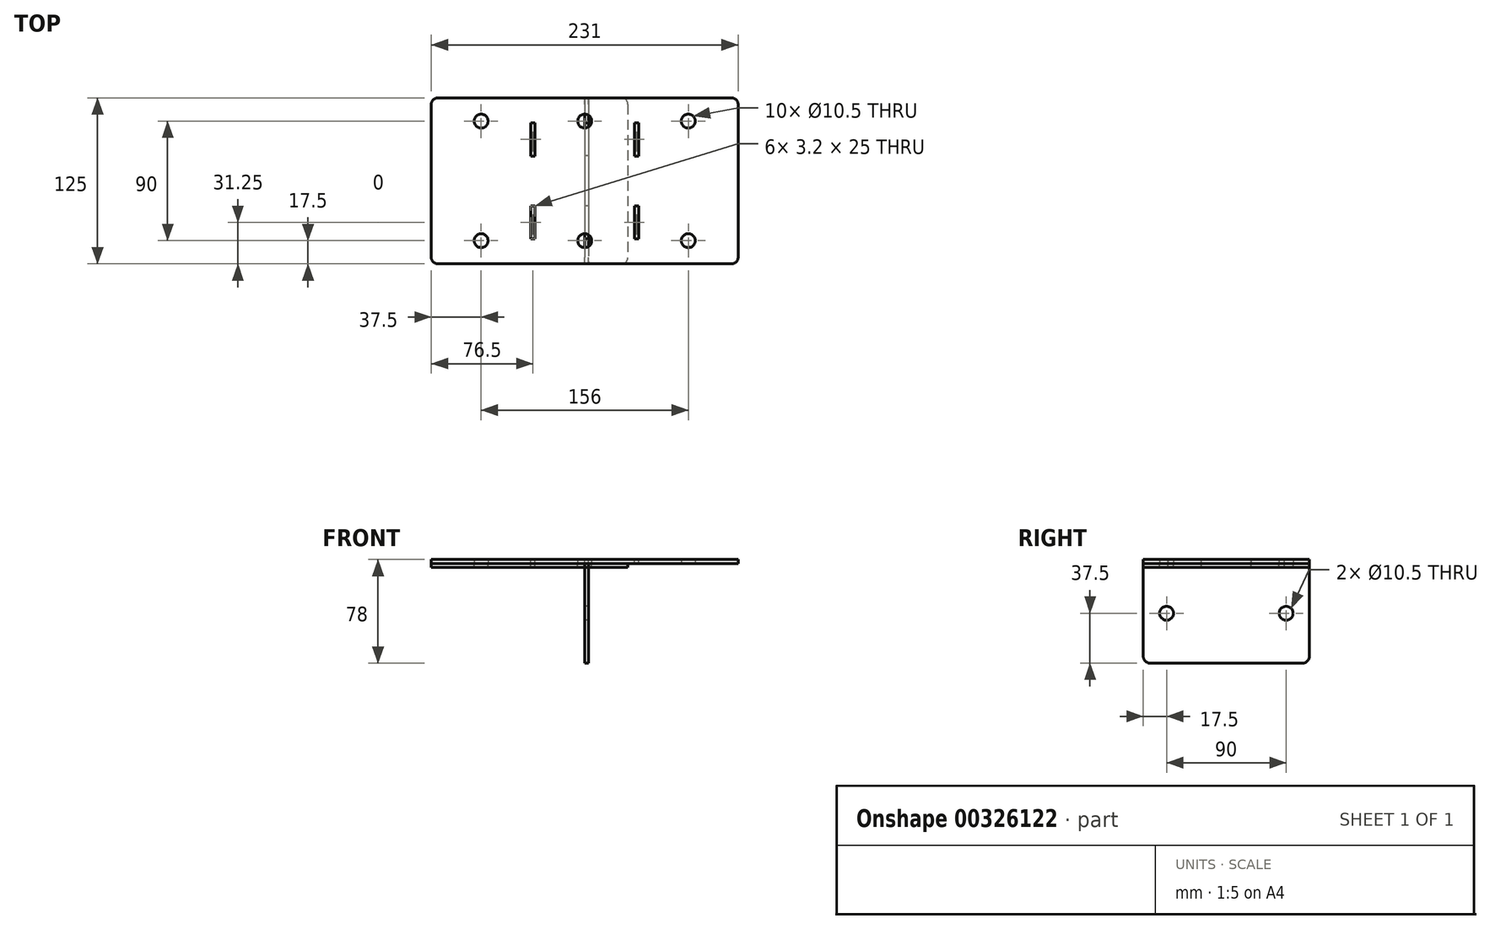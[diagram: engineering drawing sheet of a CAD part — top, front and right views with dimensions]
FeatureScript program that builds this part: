
annotation { "Feature Type Name" : "Feature", "Feature Type Description" : "" }
export const myFeature = defineFeature(function(context is Context, id is Id, definition is map)
    precondition{}
    {
        {
            var Q0;
            Q0=qCreatedBy(makeId("Top.planeOp"),FACE);
            var sketch = newSketch(context, id + "F0", { "sketchPlane" : qUnion([Q0])});
            skLineSegment(sketch, "E0.bottom", {"start": v(-115.5, 62.5) * mm, "end": v(115.5, 62.5) * mm});
            skLineSegment(sketch, "E0.top", {"start": v(-115.5, -62.5) * mm, "end": v(115.5, -62.5) * mm});
            skLineSegment(sketch, "E0.left", {"start": v(-115.5, 62.5) * mm, "end": v(-115.5, -62.5) * mm});
            skLineSegment(sketch, "E0.right", {"start": v(115.5, 62.5) * mm, "end": v(115.5, -62.5) * mm});
            skPoint(sketch, "E0.middle", {"position": v(0, 0) * mm});
            skCircle(sketch, "E1", {"center": v(0, 45) * mm, "radius": 5.25 * mm});
            skCircle(sketch, "E2", {"center": v(0, -45) * mm, "radius": 5.25 * mm});
            skCircle(sketch, "E3", {"center": v(-78, 45) * mm, "radius": 5.25 * mm});
            skCircle(sketch, "E4", {"center": v(-78, -45) * mm, "radius": 5.25 * mm});
            skCircle(sketch, "E5", {"center": v(78, 45) * mm, "radius": 5.25 * mm});
            skCircle(sketch, "E6", {"center": v(78, -45) * mm, "radius": 5.25 * mm});
            skLineSegment(sketch, "E7", {"start": v(0, 62.5) * mm, "end": v(0, -62.5) * mm});
            skLineSegment(sketch, "E8", {"start": v(-115.5, 0) * mm, "end": v(115.5, 0) * mm});
            skSolve(sketch);
        }
        {
            var Q0;
            Q0=makeQuery(id+"F0.imprint","IMPRINT",FACE,{"disambiguationData":[TD([[makeQuery(id+"F0.imprint","IMPRINT",EDGE,{"derivedFrom":sQuery(id+"F0.wireOp",EDGE,"E4")}),-1.0]])]});
            var Q1;
            Q1=makeQuery(id+"F0.imprint","IMPRINT",FACE,{"disambiguationData":[TD([[makeQuery(id+"F0.imprint","IMPRINT",EDGE,{"derivedFrom":sQuery(id+"F0.wireOp",EDGE,"E6")}),-1.0]])]});
            var Q2;
            Q2=makeQuery(id+"F0.imprint","IMPRINT",FACE,{"disambiguationData":[TD([[makeQuery(id+"F0.imprint","IMPRINT",EDGE,{"derivedFrom":sQuery(id+"F0.wireOp",EDGE,"E5")}),-1.0]])]});
            var Q3;
            Q3=makeQuery(id+"F0.imprint","IMPRINT",FACE,{"disambiguationData":[TD([[makeQuery(id+"F0.imprint","IMPRINT",EDGE,{"derivedFrom":sQuery(id+"F0.wireOp",EDGE,"E3")}),-1.0]])]});
            extrude(context, id + "F1", {"entities" : qUnion([Q0, Q1, Q2, Q3]), "depth" : 3 * mm});
        }
        {
            var Q0;
            Q0=makeQuery(id+"F1.opExtrude","CAP_FACE",FACE,{"disambiguationData":[OSD([sQuery(id+"F0.wireOp",EDGE,"E0.bottom"),sQuery(id+"F0.wireOp",EDGE,"E0.top"),sQuery(id+"F0.wireOp",EDGE,"E0.left"),sQuery(id+"F0.wireOp",EDGE,"E0.right"),sQuery(id+"F0.wireOp",EDGE,"E1"),sQuery(id+"F0.wireOp",EDGE,"E2"),sQuery(id+"F0.wireOp",EDGE,"E3"),sQuery(id+"F0.wireOp",EDGE,"E4"),sQuery(id+"F0.wireOp",EDGE,"E5"),sQuery(id+"F0.wireOp",EDGE,"E6")])],"isStart":false});
            var sketch = newSketch(context, id + "F2", { "sketchPlane" : qUnion([Q0])});
            skPoint(sketch, "E9.middle", {"position": v(0, 0) * mm});
            skLineSegment(sketch, "E10.bottom", {"start": v(-37.4, 43.75) * mm, "end": v(-40.6, 43.75) * mm});
            skLineSegment(sketch, "E10.top", {"start": v(-37.4, 18.75) * mm, "end": v(-40.6, 18.75) * mm});
            skLineSegment(sketch, "E10.left", {"start": v(-37.4, 43.75) * mm, "end": v(-37.4, 18.75) * mm});
            skLineSegment(sketch, "E10.right", {"start": v(-40.6, 43.75) * mm, "end": v(-40.6, 18.75) * mm});
            skPoint(sketch, "E10.middle", {"position": v(-39, 31.25) * mm});
            skLineSegment(sketch, "E11.MirrorCS", {"start": v(-37.4, -18.75) * mm, "end": v(-40.6, -18.75) * mm});
            skLineSegment(sketch, "E12.MirrorCS", {"start": v(-37.4, -43.75) * mm, "end": v(-40.6, -43.75) * mm});
            skLineSegment(sketch, "E13.MirrorCS", {"start": v(-37.4, -43.75) * mm, "end": v(-37.4, -18.75) * mm});
            skLineSegment(sketch, "E14.MirrorCS", {"start": v(-40.6, -43.75) * mm, "end": v(-40.6, -18.75) * mm});
            skLineSegment(sketch, "E15.MirrorCS", {"start": v(37.4, -43.75) * mm, "end": v(40.6, -43.75) * mm});
            skLineSegment(sketch, "E16.MirrorCS", {"start": v(37.4, -43.75) * mm, "end": v(37.4, -18.75) * mm});
            skLineSegment(sketch, "E17.MirrorCS", {"start": v(40.6, -43.75) * mm, "end": v(40.6, -18.75) * mm});
            skLineSegment(sketch, "E18.MirrorCS", {"start": v(37.4, -18.75) * mm, "end": v(40.6, -18.75) * mm});
            skLineSegment(sketch, "E19.MirrorCS", {"start": v(37.4, 18.75) * mm, "end": v(40.6, 18.75) * mm});
            skLineSegment(sketch, "E20.MirrorCS", {"start": v(37.4, 43.75) * mm, "end": v(37.4, 18.75) * mm});
            skLineSegment(sketch, "E21.MirrorCS", {"start": v(40.6, 43.75) * mm, "end": v(40.6, 18.75) * mm});
            skLineSegment(sketch, "E22.MirrorCS", {"start": v(37.4, 43.75) * mm, "end": v(40.6, 43.75) * mm});
            skSolve(sketch);
        }
        {
            var Q0;
            Q0=makeQuery(id+"F2.imprint","IMPRINT",FACE,{"disambiguationData":[TD([[makeQuery(id+"F2.imprint","IMPRINT",EDGE,{"derivedFrom":sQuery(id+"F2.wireOp",EDGE,"E19.MirrorCS")}),1.0]])]});
            var Q1;
            Q1=makeQuery(id+"F2.imprint","IMPRINT",FACE,{"disambiguationData":[TD([[makeQuery(id+"F2.imprint","IMPRINT",EDGE,{"derivedFrom":sQuery(id+"F2.wireOp",EDGE,"E10.bottom")}),1.0]])]});
            var Q2;
            Q2=makeQuery(id+"F2.imprint","IMPRINT",FACE,{"disambiguationData":[TD([[makeQuery(id+"F2.imprint","IMPRINT",EDGE,{"derivedFrom":sQuery(id+"F2.wireOp",EDGE,"E15.MirrorCS")}),1.0]])]});
            var Q3;
            Q3=makeQuery(id+"F2.imprint","IMPRINT",FACE,{"disambiguationData":[TD([[makeQuery(id+"F2.imprint","IMPRINT",EDGE,{"derivedFrom":sQuery(id+"F2.wireOp",EDGE,"E11.MirrorCS")}),1.0]])]});
            extrude(context, id + "F3", {"entities" : qUnion([Q0, Q1, Q2, Q3]), "operationType" : NewBodyOperationType.REMOVE, "oppositeDirection" : true, "depth" : 25 * mm});
        }
        {
            var Q0;
            Q0=makeQuery(id+"F1.opExtrude","SWEPT_EDGE",EDGE,{"disambiguationData":[OSD([sQuery(id+"F0.wireOp",EDGE,"E0.bottom"),sQuery(id+"F0.wireOp",EDGE,"E0.right")])]});
            var Q1;
            Q1=makeQuery(id+"F1.opExtrude","SWEPT_EDGE",EDGE,{"disambiguationData":[OSD([sQuery(id+"F0.wireOp",EDGE,"E0.top"),sQuery(id+"F0.wireOp",EDGE,"E0.right")])]});
            var Q2;
            Q2=makeQuery(id+"F1.opExtrude","SWEPT_EDGE",EDGE,{"disambiguationData":[OSD([sQuery(id+"F0.wireOp",EDGE,"E0.bottom"),sQuery(id+"F0.wireOp",EDGE,"E0.left")])]});
            var Q3;
            Q3=makeQuery(id+"F1.opExtrude","SWEPT_EDGE",EDGE,{"disambiguationData":[OSD([sQuery(id+"F0.wireOp",EDGE,"E0.top"),sQuery(id+"F0.wireOp",EDGE,"E0.left")])]});
            fillet(context, id + "F4", {"entities" : qUnion([Q0, Q1, Q2, Q3]), "radius" : 5 * mm, "tangentPropagation" : true, "allowEdgeOverflow" : false});
        }
        {
            var Q0;
            Q0=qCreatedBy(makeId("Right.planeOp"),FACE);
            var sketch = newSketch(context, id + "F5", { "sketchPlane" : qUnion([Q0])});
            skLineSegment(sketch, "E23", {"start": v(0, 0) * mm, "end": v(0, -37.5) * mm, "construction": true});
            skLineSegment(sketch, "E24.bottom", {"start": v(62.5, 0) * mm, "end": v(43.65, 0) * mm});
            skLineSegment(sketch, "E24.top", {"start": v(62.5, -75) * mm, "end": v(-62.5, -75) * mm});
            skLineSegment(sketch, "E24.left", {"start": v(62.5, 0) * mm, "end": v(62.5, -75) * mm});
            skLineSegment(sketch, "E24.right", {"start": v(-62.5, 0) * mm, "end": v(-62.5, -75) * mm});
            skPoint(sketch, "E24.middle", {"position": v(0, -37.5) * mm});
            skPoint(sketch, "E25.0", {"position": v(31.25, 0) * mm});
            skPoint(sketch, "E25.1", {"position": v(-31.25, 0) * mm});
            skLineSegment(sketch, "E26", {"start": v(31.25, 0) * mm, "end": v(31.25, 1.4) * mm});
            skLineSegment(sketch, "E27", {"start": v(-31.25, 0) * mm, "end": v(-31.25, 1.4) * mm});
            skLineSegment(sketch, "E28.top", {"start": v(43.65, 2.8) * mm, "end": v(18.85, 2.8) * mm});
            skLineSegment(sketch, "E28.left", {"start": v(43.65, 0) * mm, "end": v(43.65, 2.8) * mm});
            skLineSegment(sketch, "E28.right", {"start": v(18.85, 0) * mm, "end": v(18.85, 2.8) * mm});
            skPoint(sketch, "E28.middle", {"position": v(31.25, 1.4) * mm});
            skLineSegment(sketch, "E29.top", {"start": v(-18.85, 2.8) * mm, "end": v(-43.65, 2.8) * mm});
            skLineSegment(sketch, "E29.left", {"start": v(-18.85, 0) * mm, "end": v(-18.85, 2.8) * mm});
            skLineSegment(sketch, "E29.right", {"start": v(-43.65, 0) * mm, "end": v(-43.65, 2.8) * mm});
            skPoint(sketch, "E29.middle", {"position": v(-31.25, 1.4) * mm});
            skLineSegment(sketch, "E30.trimOffspring", {"start": v(18.85, 0) * mm, "end": v(-18.85, 0) * mm});
            skLineSegment(sketch, "E31.trimOffspring", {"start": v(-43.65, 0) * mm, "end": v(-62.5, 0) * mm});
            skLineSegment(sketch, "E32", {"start": v(0, -37.5) * mm, "end": v(45, -37.5) * mm});
            skCircle(sketch, "E33", {"center": v(45, -37.5) * mm, "radius": 5.25 * mm});
            skCircle(sketch, "E34.MirrorC", {"center": v(-45, -37.5) * mm, "radius": 5.25 * mm});
            skSolve(sketch);
        }
        {
            var Q0;
            Q0=makeQuery(id+"F5.imprint","IMPRINT",FACE,{"disambiguationData":[TD([[makeQuery(id+"F5.imprint","IMPRINT",EDGE,{"derivedFrom":sQuery(id+"F5.wireOp",EDGE,"E24.bottom")}),1.0]])]});
            extrude(context, id + "F6", {"entities" : qUnion([Q0]), "depth" : 3 * mm});
        }
        {
            var Q0;
            Q0=makeQuery(id+"F6.opExtrude","SWEPT_EDGE",EDGE,{"disambiguationData":[OSD([sQuery(id+"F5.wireOp",EDGE,"E24.top"),sQuery(id+"F5.wireOp",EDGE,"E24.left")])]});
            var Q1;
            Q1=makeQuery(id+"F6.opExtrude","SWEPT_EDGE",EDGE,{"disambiguationData":[OSD([sQuery(id+"F5.wireOp",EDGE,"E24.top"),sQuery(id+"F5.wireOp",EDGE,"E24.right")])]});
            fillet(context, id + "F7", {"entities" : qUnion([Q0, Q1]), "radius" : 5 * mm, "tangentPropagation" : true, "allowEdgeOverflow" : false});
        }
        {
            var Q0;
            Q0=qCreatedBy(makeId("Top.planeOp"),FACE);
            var sketch = newSketch(context, id + "F8", { "sketchPlane" : qUnion([Q0])});
            skLineSegment(sketch, "E35.0", {"start": v(-110.5, 62.5) * mm, "end": v(27.5, 62.5) * mm});
            skLineSegment(sketch, "E36.0", {"start": v(-115.5, 57.5) * mm, "end": v(-115.5, -57.5) * mm});
            skLineSegment(sketch, "E37.0", {"start": v(-110.5, -62.5) * mm, "end": v(27.5, -62.5) * mm});
            skArc(sketch, "E38.0", {"start": v(-115.5, 57.5) * mm, "mid": v(-114.04, 61.04) * mm, "end": v(-110.5, 62.5) * mm});
            skArc(sketch, "E39.0", {"start": v(-110.5, -62.5) * mm, "mid": v(-114.04, -61.04) * mm, "end": v(-115.5, -57.5) * mm});
            skCircle(sketch, "E40.0", {"center": v(-78, 45) * mm, "radius": 5.25 * mm});
            skCircle(sketch, "E41.0", {"center": v(-78, -45) * mm, "radius": 5.25 * mm});
            skLineSegment(sketch, "E42.0", {"start": v(-40.6, -43.75) * mm, "end": v(-40.6, -18.75) * mm});
            skLineSegment(sketch, "E43.0", {"start": v(-37.4, -43.75) * mm, "end": v(-37.4, -18.75) * mm});
            skLineSegment(sketch, "E44.0", {"start": v(-37.4, -18.75) * mm, "end": v(-40.6, -18.75) * mm});
            skLineSegment(sketch, "E45.0", {"start": v(-37.4, -43.75) * mm, "end": v(-40.6, -43.75) * mm});
            skLineSegment(sketch, "E46.0", {"start": v(-37.4, 18.75) * mm, "end": v(-40.6, 18.75) * mm});
            skLineSegment(sketch, "E47.0", {"start": v(-40.6, 43.75) * mm, "end": v(-40.6, 18.75) * mm});
            skLineSegment(sketch, "E48.0", {"start": v(-37.4, 43.75) * mm, "end": v(-37.4, 18.75) * mm});
            skLineSegment(sketch, "E49.0", {"start": v(-37.4, 43.75) * mm, "end": v(-40.6, 43.75) * mm});
            skCircle(sketch, "E50.0", {"center": v(0, 45) * mm, "radius": 5.25 * mm});
            skCircle(sketch, "E51.0", {"center": v(0, -45) * mm, "radius": 5.25 * mm});
            skLineSegment(sketch, "E52", {"start": v(0, 0) * mm, "end": v(32.5, 0) * mm});
            skLineSegment(sketch, "E53", {"start": v(32.5, 0) * mm, "end": v(32.5, 57.5) * mm});
            skLineSegment(sketch, "E54", {"start": v(32.5, 0) * mm, "end": v(32.5, -57.5) * mm});
            skPoint(sketch, "E55.newPointB", {"position": v(110.5, 62.5) * mm});
            skArc(sketch, "E55.filletArc", {"start": v(32.5, 57.5) * mm, "mid": v(31.04, 61.04) * mm, "end": v(27.5, 62.5) * mm});
            skPoint(sketch, "E56.newPointB", {"position": v(110.5, -62.5) * mm});
            skArc(sketch, "E56.filletArc", {"start": v(27.5, -62.5) * mm, "mid": v(31.04, -61.04) * mm, "end": v(32.5, -57.5) * mm});
            skSolve(sketch);
        }
        {
            var Q0;
            Q0=makeQuery(id+"F8.imprint","IMPRINT",FACE,{"disambiguationData":[TD([[makeQuery(id+"F8.imprint","IMPRINT",EDGE,{"derivedFrom":sQuery(id+"F8.wireOp",EDGE,"E35.0")}),-1.0]])]});
            extrude(context, id + "F9", {"entities" : qUnion([Q0]), "oppositeDirection" : true, "depth" : 3 * mm});
        }
    });
